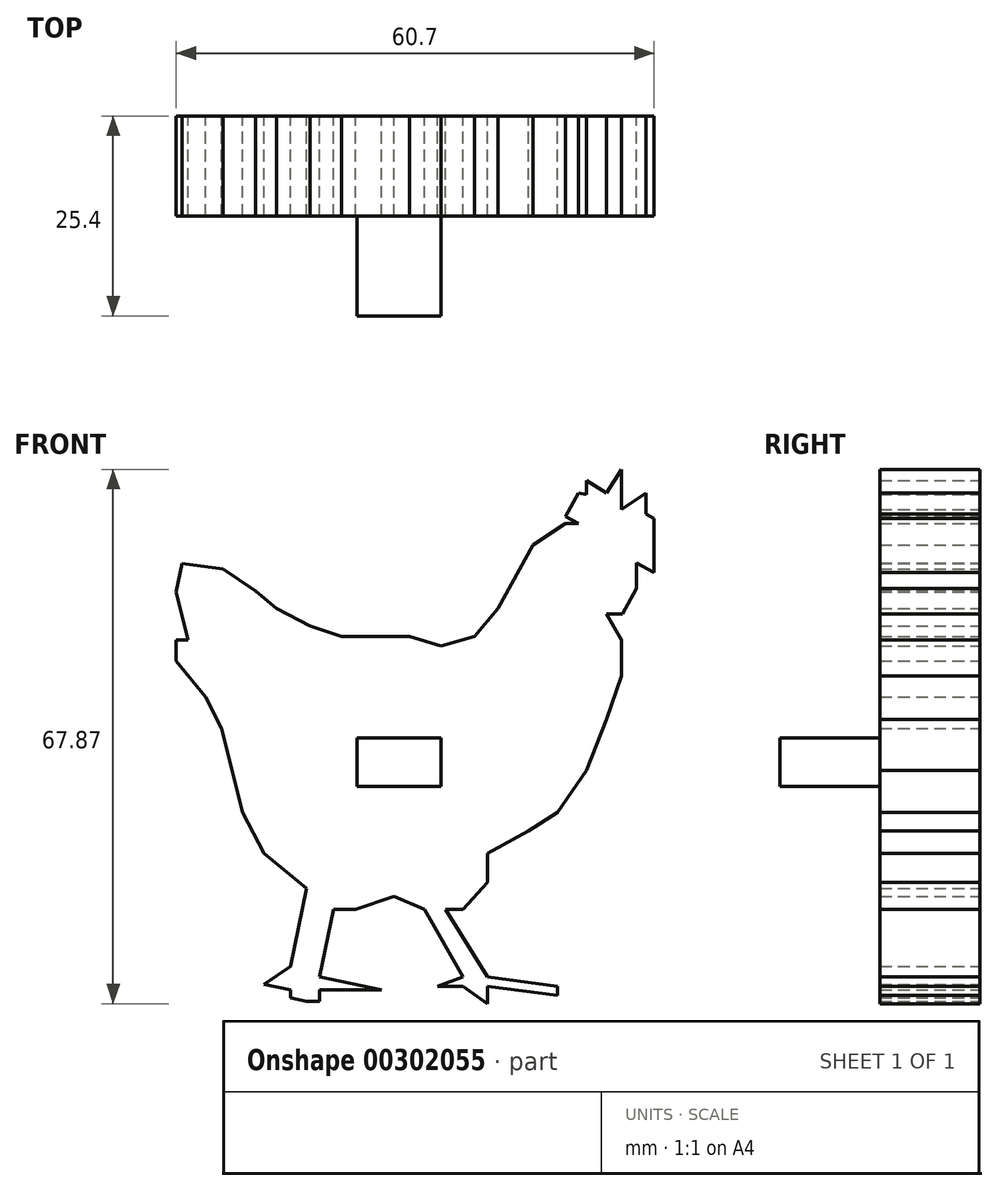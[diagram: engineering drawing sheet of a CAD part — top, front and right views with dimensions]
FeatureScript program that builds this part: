
annotation { "Feature Type Name" : "Feature", "Feature Type Description" : "" }
export const myFeature = defineFeature(function(context is Context, id is Id, definition is map)
    precondition{}
    {
        {
            var Q0;
            Q0=qCreatedBy(makeId("Front.planeOp"),FACE);
            var sketch = newSketch(context, id + "F0", { "sketchPlane" : qUnion([Q0])});
            skLineSegment(sketch, "E0", {"start": v(-136.27, 19.24) * mm, "end": v(-132.12, 16.42) * mm});
            skLineSegment(sketch, "E1", {"start": v(-132.12, 16.42) * mm, "end": v(-129.46, 14.2) * mm});
            skLineSegment(sketch, "E2", {"start": v(-129.46, 14.2) * mm, "end": v(-125.16, 11.98) * mm});
            skLineSegment(sketch, "E3", {"start": v(-125.16, 11.98) * mm, "end": v(-121.16, 10.65) * mm});
            skLineSegment(sketch, "E4", {"start": v(-121.16, 10.65) * mm, "end": v(-117.46, 10.65) * mm});
            skLineSegment(sketch, "E5", {"start": v(-117.46, 10.65) * mm, "end": v(-112.58, 10.65) * mm});
            skLineSegment(sketch, "E6", {"start": v(-112.58, 10.65) * mm, "end": v(-108.58, 9.46) * mm});
            skLineSegment(sketch, "E7", {"start": v(-108.58, 9.46) * mm, "end": v(-104.28, 10.65) * mm});
            skLineSegment(sketch, "E8", {"start": v(-104.28, 10.65) * mm, "end": v(-101.32, 14.2) * mm});
            skLineSegment(sketch, "E9", {"start": v(-101.32, 14.2) * mm, "end": v(-98.8, 18.8) * mm});
            skLineSegment(sketch, "E10", {"start": v(-98.8, 18.8) * mm, "end": v(-96.88, 22.3) * mm});
            skLineSegment(sketch, "E11", {"start": v(-96.88, 22.3) * mm, "end": v(-92.73, 25.01) * mm});
            skLineSegment(sketch, "E12", {"start": v(-92.73, 25.01) * mm, "end": v(-91.1, 25.01) * mm});
            skLineSegment(sketch, "E13", {"start": v(-91.1, 25.01) * mm, "end": v(-92.73, 25.9) * mm});
            skLineSegment(sketch, "E14", {"start": v(-92.73, 25.9) * mm, "end": v(-91.1, 28.88) * mm});
            skLineSegment(sketch, "E15", {"start": v(-82.52, 28.88) * mm, "end": v(-82.52, 26.2) * mm});
            skLineSegment(sketch, "E16", {"start": v(-82.52, 26.2) * mm, "end": v(-81.5, 25.63) * mm});
            skLineSegment(sketch, "E17", {"start": v(-81.5, 25.63) * mm, "end": v(-81.5, 20.87) * mm});
            skLineSegment(sketch, "E18", {"start": v(-81.5, 20.87) * mm, "end": v(-81.5, 18.8) * mm});
            skLineSegment(sketch, "E19", {"start": v(-81.5, 18.8) * mm, "end": v(-83.72, 20.01) * mm});
            skLineSegment(sketch, "E20", {"start": v(-83.72, 20.01) * mm, "end": v(-83.72, 16.72) * mm});
            skLineSegment(sketch, "E21", {"start": v(-83.72, 16.72) * mm, "end": v(-85.48, 13.51) * mm});
            skLineSegment(sketch, "E22", {"start": v(-85.48, 13.51) * mm, "end": v(-87.53, 13.51) * mm});
            skLineSegment(sketch, "E23", {"start": v(-87.53, 13.51) * mm, "end": v(-85.62, 10.2) * mm});
            skLineSegment(sketch, "E24", {"start": v(-85.62, 10.2) * mm, "end": v(-85.62, 5.61) * mm});
            skLineSegment(sketch, "E25", {"start": v(-85.62, 5.61) * mm, "end": v(-87.53, 0.13) * mm});
            skLineSegment(sketch, "E26", {"start": v(-87.53, 0.13) * mm, "end": v(-90.07, -6.38) * mm});
            skLineSegment(sketch, "E27", {"start": v(-90.07, -6.38) * mm, "end": v(-93.77, -11.71) * mm});
            skLineSegment(sketch, "E28", {"start": v(-93.77, -11.71) * mm, "end": v(-97.47, -14.08) * mm});
            skLineSegment(sketch, "E29", {"start": v(-97.47, -14.08) * mm, "end": v(-102.65, -16.9) * mm});
            skLineSegment(sketch, "E30", {"start": v(-102.65, -16.9) * mm, "end": v(-102.65, -20.6) * mm});
            skLineSegment(sketch, "E31", {"start": v(-102.65, -20.6) * mm, "end": v(-105.76, -24) * mm});
            skLineSegment(sketch, "E32", {"start": v(-105.76, -24) * mm, "end": v(-107.99, -24) * mm});
            skLineSegment(sketch, "E33", {"start": v(-107.99, -24) * mm, "end": v(-102.65, -32.6) * mm});
            skLineSegment(sketch, "E34", {"start": v(-102.65, -32.6) * mm, "end": v(-93.77, -33.78) * mm});
            skLineSegment(sketch, "E35", {"start": v(-93.77, -33.78) * mm, "end": v(-93.77, -34.96) * mm});
            skLineSegment(sketch, "E36", {"start": v(-93.77, -34.96) * mm, "end": v(-102.65, -33.78) * mm});
            skLineSegment(sketch, "E37", {"start": v(-102.65, -33.78) * mm, "end": v(-102.65, -36) * mm});
            skLineSegment(sketch, "E38", {"start": v(-102.65, -36) * mm, "end": v(-105.76, -33.78) * mm});
            skLineSegment(sketch, "E39", {"start": v(-105.76, -33.78) * mm, "end": v(-109.02, -33.78) * mm});
            skLineSegment(sketch, "E40", {"start": v(-109.02, -33.78) * mm, "end": v(-105.76, -32.6) * mm});
            skLineSegment(sketch, "E41", {"start": v(-105.76, -32.6) * mm, "end": v(-110.65, -24) * mm});
            skLineSegment(sketch, "E42", {"start": v(-110.65, -24) * mm, "end": v(-114.5, -22.37) * mm});
            skLineSegment(sketch, "E43", {"start": v(-114.5, -22.37) * mm, "end": v(-119.39, -24) * mm});
            skLineSegment(sketch, "E44", {"start": v(-119.39, -24) * mm, "end": v(-122.2, -24) * mm});
            skLineSegment(sketch, "E45", {"start": v(-122.2, -24) * mm, "end": v(-123.98, -32.6) * mm});
            skLineSegment(sketch, "E46", {"start": v(-123.98, -32.6) * mm, "end": v(-116.13, -34.22) * mm});
            skLineSegment(sketch, "E47", {"start": v(-123.98, -34.22) * mm, "end": v(-116.13, -34.22) * mm});
            skLineSegment(sketch, "E48", {"start": v(-123.98, -35.7) * mm, "end": v(-125.6, -35.7) * mm});
            skLineSegment(sketch, "E49", {"start": v(-125.6, -35.7) * mm, "end": v(-127.66, -35.28) * mm});
            skLineSegment(sketch, "E50", {"start": v(-127.66, -35.28) * mm, "end": v(-127.66, -34.22) * mm});
            skLineSegment(sketch, "E51", {"start": v(-127.66, -34.22) * mm, "end": v(-131, -33.52) * mm});
            skLineSegment(sketch, "E52", {"start": v(-131, -33.52) * mm, "end": v(-127.66, -31.26) * mm});
            skLineSegment(sketch, "E53", {"start": v(-127.66, -31.26) * mm, "end": v(-125.6, -21.34) * mm});
            skLineSegment(sketch, "E54", {"start": v(-125.6, -21.34) * mm, "end": v(-131, -16.9) * mm});
            skLineSegment(sketch, "E55", {"start": v(-131, -16.9) * mm, "end": v(-133.75, -11.71) * mm});
            skLineSegment(sketch, "E56", {"start": v(-133.75, -11.71) * mm, "end": v(-135.08, -6.38) * mm});
            skLineSegment(sketch, "E57", {"start": v(-135.08, -6.38) * mm, "end": v(-136.42, -1.05) * mm});
            skLineSegment(sketch, "E58", {"start": v(-136.42, -1.05) * mm, "end": v(-138.49, 2.95) * mm});
            skLineSegment(sketch, "E59", {"start": v(-138.49, 2.95) * mm, "end": v(-142.2, 7.54) * mm});
            skLineSegment(sketch, "E60", {"start": v(-142.2, 7.54) * mm, "end": v(-142.2, 10.2) * mm});
            skLineSegment(sketch, "E61", {"start": v(-142.2, 10.2) * mm, "end": v(-140.71, 10.2) * mm});
            skLineSegment(sketch, "E62", {"start": v(-140.71, 10.2) * mm, "end": v(-142.2, 16.28) * mm});
            skLineSegment(sketch, "E63", {"start": v(-142.2, 16.28) * mm, "end": v(-141.44, 19.89) * mm});
            skLineSegment(sketch, "E64", {"start": v(-141.44, 19.89) * mm, "end": v(-136.27, 19.24) * mm});
            skLineSegment(sketch, "E65", {"start": v(-91.1, 28.88) * mm, "end": v(-90.07, 28.66) * mm});
            skLineSegment(sketch, "E66", {"start": v(-90.07, 28.66) * mm, "end": v(-90.07, 30.5) * mm});
            skLineSegment(sketch, "E67", {"start": v(-90.07, 30.5) * mm, "end": v(-87.53, 28.88) * mm});
            skLineSegment(sketch, "E68", {"start": v(-87.53, 28.88) * mm, "end": v(-85.62, 31.87) * mm});
            skLineSegment(sketch, "E69", {"start": v(-85.62, 31.87) * mm, "end": v(-85.62, 26.79) * mm});
            skLineSegment(sketch, "E70", {"start": v(-85.62, 26.79) * mm, "end": v(-82.52, 28.88) * mm});
            skLineSegment(sketch, "E71", {"start": v(-123.98, -34.22) * mm, "end": v(-123.98, -35.7) * mm});
            skSolve(sketch);
        }
        {
            var Q0;
            Q0=makeQuery(id+"F0.imprint","IMPRINT",FACE,{"disambiguationData":[TD([[makeQuery(id+"F0.imprint","IMPRINT",EDGE,{"derivedFrom":sQuery(id+"F0.wireOp",EDGE,"E0")}),-1.0]])]});
            extrude(context, id + "F1", {"entities" : qUnion([Q0]), "depth" : 12.7 * mm});
        }
        {
            var Q0;
            Q0=makeQuery(id+"F1.opExtrude","CAP_FACE",FACE,{"disambiguationData":[OSD([sQuery(id+"F0.wireOp",EDGE,"E0"),sQuery(id+"F0.wireOp",EDGE,"E1"),sQuery(id+"F0.wireOp",EDGE,"E2"),sQuery(id+"F0.wireOp",EDGE,"E3"),sQuery(id+"F0.wireOp",EDGE,"E4"),sQuery(id+"F0.wireOp",EDGE,"E5"),sQuery(id+"F0.wireOp",EDGE,"E6"),sQuery(id+"F0.wireOp",EDGE,"E7"),sQuery(id+"F0.wireOp",EDGE,"E8"),sQuery(id+"F0.wireOp",EDGE,"E9"),sQuery(id+"F0.wireOp",EDGE,"E10"),sQuery(id+"F0.wireOp",EDGE,"E11"),sQuery(id+"F0.wireOp",EDGE,"E12"),sQuery(id+"F0.wireOp",EDGE,"E13"),sQuery(id+"F0.wireOp",EDGE,"E14"),sQuery(id+"F0.wireOp",EDGE,"E15"),sQuery(id+"F0.wireOp",EDGE,"E16"),sQuery(id+"F0.wireOp",EDGE,"E17"),sQuery(id+"F0.wireOp",EDGE,"E18"),sQuery(id+"F0.wireOp",EDGE,"E19"),sQuery(id+"F0.wireOp",EDGE,"E20"),sQuery(id+"F0.wireOp",EDGE,"E21"),sQuery(id+"F0.wireOp",EDGE,"E22"),sQuery(id+"F0.wireOp",EDGE,"E23"),sQuery(id+"F0.wireOp",EDGE,"E24"),sQuery(id+"F0.wireOp",EDGE,"E25"),sQuery(id+"F0.wireOp",EDGE,"E26"),sQuery(id+"F0.wireOp",EDGE,"E27"),sQuery(id+"F0.wireOp",EDGE,"E28"),sQuery(id+"F0.wireOp",EDGE,"E29"),sQuery(id+"F0.wireOp",EDGE,"E30"),sQuery(id+"F0.wireOp",EDGE,"E31"),sQuery(id+"F0.wireOp",EDGE,"E32"),sQuery(id+"F0.wireOp",EDGE,"E33"),sQuery(id+"F0.wireOp",EDGE,"E34"),sQuery(id+"F0.wireOp",EDGE,"E35"),sQuery(id+"F0.wireOp",EDGE,"E36"),sQuery(id+"F0.wireOp",EDGE,"E37"),sQuery(id+"F0.wireOp",EDGE,"E38"),sQuery(id+"F0.wireOp",EDGE,"E39"),sQuery(id+"F0.wireOp",EDGE,"E40"),sQuery(id+"F0.wireOp",EDGE,"E41"),sQuery(id+"F0.wireOp",EDGE,"E42"),sQuery(id+"F0.wireOp",EDGE,"E43"),sQuery(id+"F0.wireOp",EDGE,"E44"),sQuery(id+"F0.wireOp",EDGE,"E45"),sQuery(id+"F0.wireOp",EDGE,"E46"),sQuery(id+"F0.wireOp",EDGE,"E47"),sQuery(id+"F0.wireOp",EDGE,"E48"),sQuery(id+"F0.wireOp",EDGE,"E49"),sQuery(id+"F0.wireOp",EDGE,"E50"),sQuery(id+"F0.wireOp",EDGE,"E51"),sQuery(id+"F0.wireOp",EDGE,"E52"),sQuery(id+"F0.wireOp",EDGE,"E53"),sQuery(id+"F0.wireOp",EDGE,"E54"),sQuery(id+"F0.wireOp",EDGE,"E55"),sQuery(id+"F0.wireOp",EDGE,"E56"),sQuery(id+"F0.wireOp",EDGE,"E57"),sQuery(id+"F0.wireOp",EDGE,"E58"),sQuery(id+"F0.wireOp",EDGE,"E59"),sQuery(id+"F0.wireOp",EDGE,"E60"),sQuery(id+"F0.wireOp",EDGE,"E61"),sQuery(id+"F0.wireOp",EDGE,"E62"),sQuery(id+"F0.wireOp",EDGE,"E63"),sQuery(id+"F0.wireOp",EDGE,"E64"),sQuery(id+"F0.wireOp",EDGE,"E65"),sQuery(id+"F0.wireOp",EDGE,"E66"),sQuery(id+"F0.wireOp",EDGE,"E67"),sQuery(id+"F0.wireOp",EDGE,"E68"),sQuery(id+"F0.wireOp",EDGE,"E69"),sQuery(id+"F0.wireOp",EDGE,"E70"),sQuery(id+"F0.wireOp",EDGE,"E71")])],"isStart":false});
            var sketch = newSketch(context, id + "F2", { "sketchPlane" : qUnion([Q0])});
            skLineSegment(sketch, "E72", {"start": v(-108.57, -4.43) * mm, "end": v(-108.57, -2.22) * mm});
            skLineSegment(sketch, "E73", {"start": v(-108.57, -2.22) * mm, "end": v(-119.21, -2.22) * mm});
            skLineSegment(sketch, "E74", {"start": v(-119.21, -2.22) * mm, "end": v(-119.21, -4.43) * mm});
            skLineSegment(sketch, "E75", {"start": v(-119.21, -4.43) * mm, "end": v(-119.21, -8.42) * mm});
            skLineSegment(sketch, "E76", {"start": v(-119.21, -8.42) * mm, "end": v(-108.57, -8.42) * mm});
            skLineSegment(sketch, "E77", {"start": v(-108.57, -8.42) * mm, "end": v(-108.57, -4.43) * mm});
            skSolve(sketch);
        }
        {
            var Q0;
            Q0 = qSketchRegion(id + "F2", true);
            extrude(context, id + "F3", {"entities" : qUnion([Q0]), "operationType" : NewBodyOperationType.ADD, "depth" : 12.7 * mm});
        }
    });
